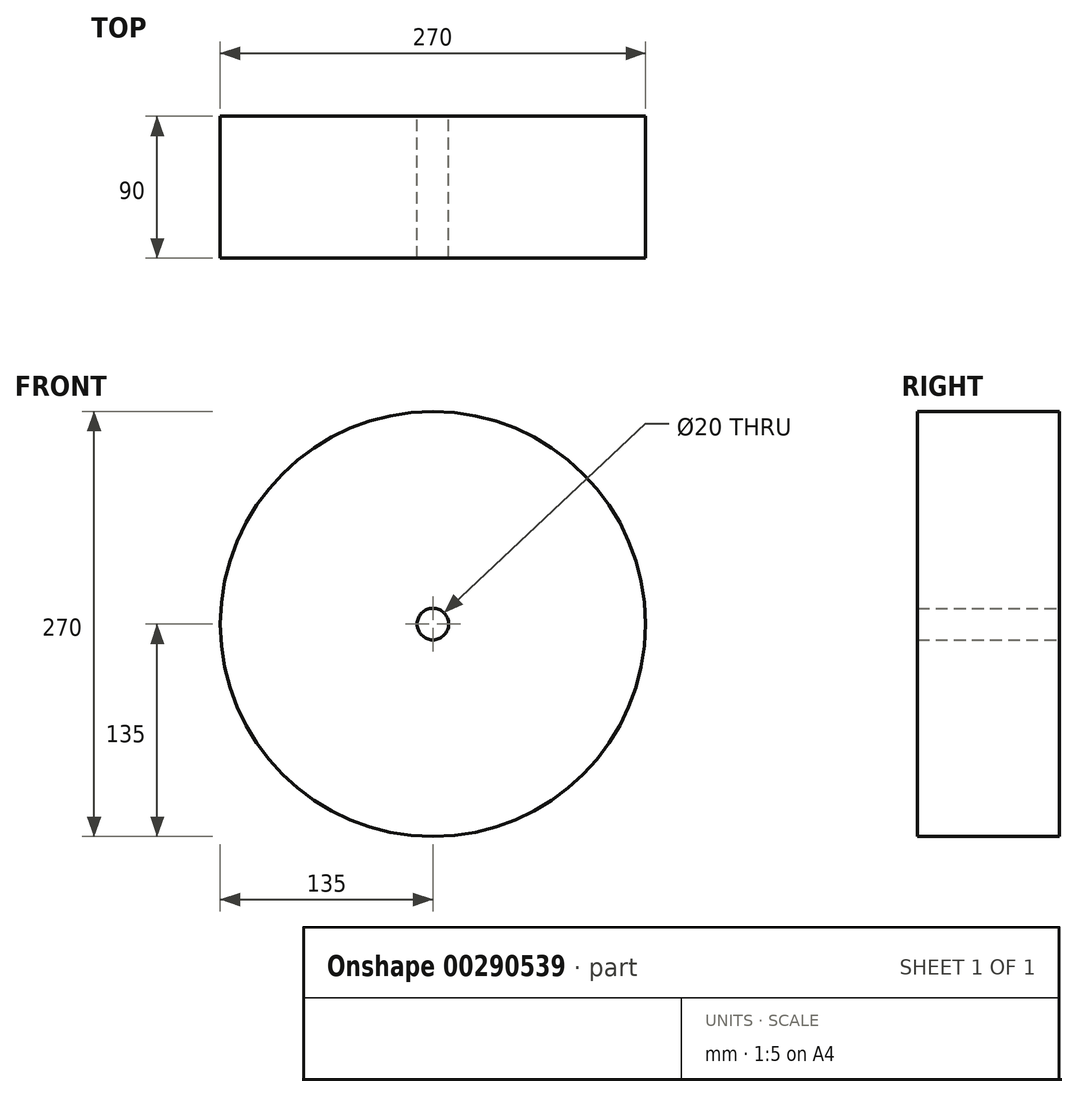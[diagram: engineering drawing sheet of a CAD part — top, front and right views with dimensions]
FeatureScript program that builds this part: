
annotation { "Feature Type Name" : "Feature", "Feature Type Description" : "" }
export const myFeature = defineFeature(function(context is Context, id is Id, definition is map)
    precondition{}
    {
        {
            var Q0;
            Q0=qCreatedBy(makeId("Front.planeOp"),FACE);
            var sketch = newSketch(context, id + "F0", { "sketchPlane" : qUnion([Q0])});
            skCircle(sketch, "E0", {"center": v(0, 0) * mm, "radius": 135 * mm});
            skCircle(sketch, "E1", {"center": v(0, 0) * mm, "radius": 10 * mm});
            skSolve(sketch);
        }
        {
            var Q0;
            Q0=makeQuery(id+"F0.imprint","IMPRINT",FACE,{"disambiguationData":[TD([[makeQuery(id+"F0.imprint","IMPRINT",EDGE,{"derivedFrom":sQuery(id+"F0.wireOp",EDGE,"E0")}),1.0]])]});
            extrude(context, id + "F1", {"entities" : qUnion([Q0]), "depth" : 90 * mm});
        }
    });
